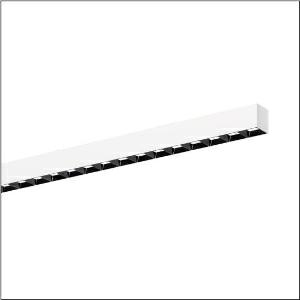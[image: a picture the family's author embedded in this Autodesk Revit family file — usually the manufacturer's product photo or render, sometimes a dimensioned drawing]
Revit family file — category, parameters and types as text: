
# Revit family: silica_r__21_51mx22da44wb_17fd
name_source: partatom
category: Lighting Fixtures
units: mm (PartAtom-declared; Revit-internal decimal feet)

## family parameters
Cut with Voids When Loaded = No
Host = Face
Light Source = No
Part Type = Normal
Room Calculation Point = No
Round Connector Dimension = Use Diameter
Shared = No

## types (1)
- --- (1 x LED, 4320 lm, 25.6 W, 4000K)
    Apparent Load = 26 VA
    CIE Flux Codes = 86 100 100 100 100
    Color Rendering = 80
    Color Temperature = 4000K
    Default Elevation = 1800 mm
    Description = Silica® 21, office luminaire, primary light control with darklight reflector, of PMMA, black, CAT 2 (L<= 3000cd/m²), light emission: direct distribution, primary light characteristic: symmetric, installation type: surface-mounted, LED, rated luminous flux: 4.320lm, luminous efficacy: 169lm/W, light colour: 840, colour temperature: 4000K, with terminal, 3+2-pole, max. 2.5mm², mains connection: 220..240V, AC, 50/60Hz, rated input power: 25.6W, luminaire housing, of aluminium, traffic white (RAL 9016), length: 1.204mm, width: 53mm, height: 53mm, protection rating (complete): IP20, insulation class (complete): insulation class I (protective earthing), certification: CE, permissible operating ambient temperature: 0..+35°C, standard: EN 50419, packaging unit: 1 piece
    Height = 0 mm  [stored 0 ft]
    Lamp = 1 x LED
    Lamp Light Flux = 4320 lm
    Lamp Power = 25.6 W
    Lamp count = 1
    Length = 1204 mm
    Luminous efficacy = 169 lm/W
    Manufacturer = Siteco
    ModVariant = No
    Model = 51MX22DA44WB
    Mounting Place = Ceiling
    Mounting Type = Recessed
    Number of Poles = 1
    OnlyDefault = Yes
    Power Factor = 1
    Product Name = Silica® 21
    Product group = office luminaire | ceiling recessed
    ProductGroupID = 401
    Protection Class = Protection class I
    Protection Degree = IP 20
    RLX_Detail_Level = 1
    RLX_Emergency_Light_Flux = 0 lm
    RLX_Emergency_Type = 0
    RLX_Emergency_Type_DB = No
    RlxData = <blob elided: 41277 chars, md5=ab0f0f14>
    Socket = socket
    Standby Power = 0 W
    System Light Flux = 4320 lm
    System Power = 26 W
    Type Comments = factory setting: luminous flux: 100 % | dim-lin: 254 | 367 mA
    Type Image = l_1297779.jpg
    URL = http://relux.com
    VarID = @adj_056501
    Voltage = 0 V
    Weight = 0.00 kg
    Width = 53 mm

note: [stored X ft] marks values corroborated as IEEE doubles in the binary element streams (Revit-internal decimal feet)

## geometry (parser evidence)
native form markers: Blend x4, Sweep x9
no freeform markers — native parametric forms only
